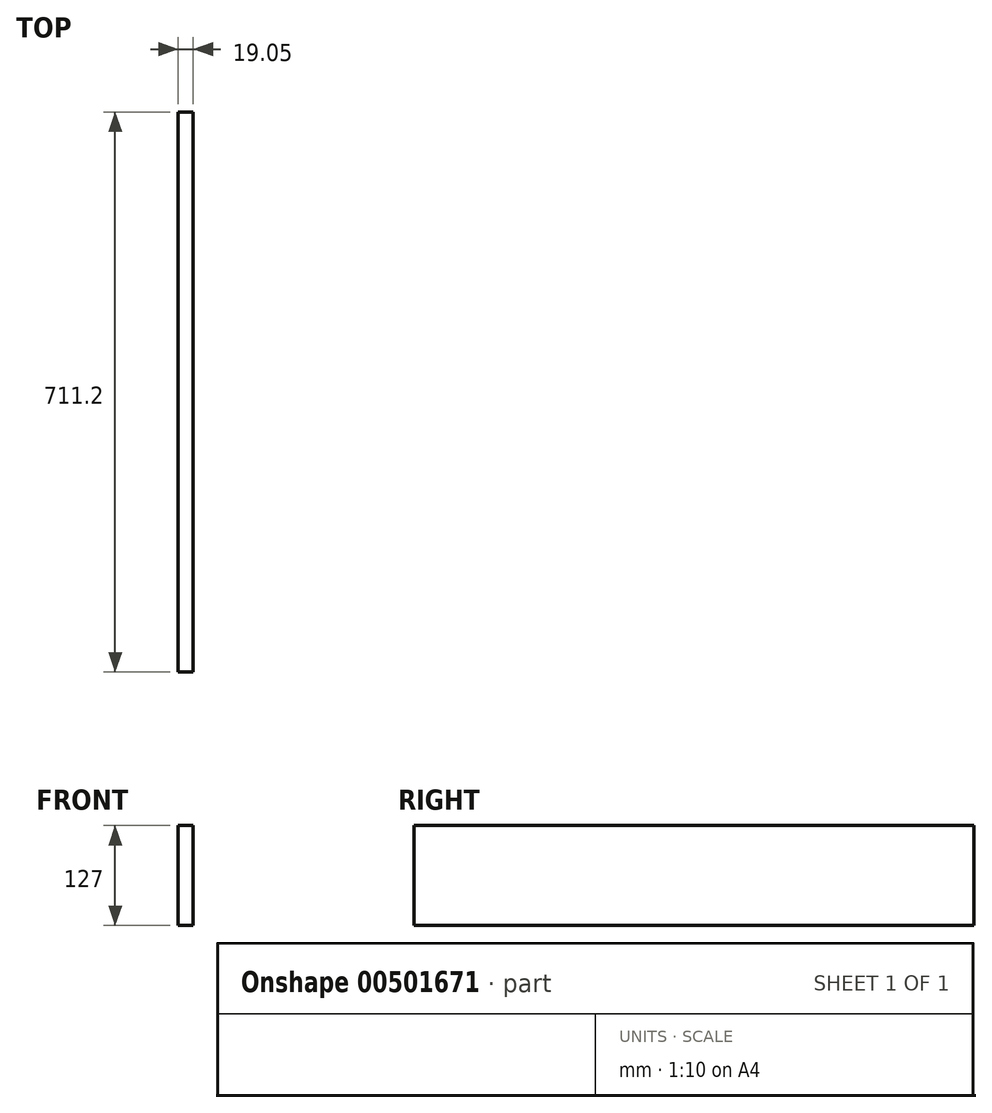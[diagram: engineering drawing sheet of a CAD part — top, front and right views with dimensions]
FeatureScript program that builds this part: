
annotation { "Feature Type Name" : "Feature", "Feature Type Description" : "" }
export const myFeature = defineFeature(function(context is Context, id is Id, definition is map)
    precondition{}
    {
        {
            var Q0;
            Q0=qCreatedBy(makeId("Right.planeOp"),FACE);
            var sketch = newSketch(context, id + "F0", { "sketchPlane" : qUnion([Q0])});
            skLineSegment(sketch, "E0.bottom", {"start": v(0, 0) * mm, "end": v(711.2, 0) * mm});
            skLineSegment(sketch, "E0.top", {"start": v(0, 127) * mm, "end": v(711.2, 127) * mm});
            skLineSegment(sketch, "E0.left", {"start": v(0, 0) * mm, "end": v(0, 127) * mm});
            skLineSegment(sketch, "E0.right", {"start": v(711.2, 0) * mm, "end": v(711.2, 127) * mm});
            skSolve(sketch);
        }
        {
            var Q0;
            Q0=makeQuery(id+"F0.imprint","IMPRINT",FACE,{"disambiguationData":[TD([[makeQuery(id+"F0.imprint","IMPRINT",EDGE,{"derivedFrom":sQuery(id+"F0.wireOp",EDGE,"E0.bottom")}),1.0]])]});
            extrude(context, id + "F1", {"entities" : qUnion([Q0]), "depth" : 19.05 * mm});
        }
    });
